# Revit family: HOSPIVAC 3 SIRELLA
name_source: partatom
category: Equipement de génie climatique
revit_build: Autodesk Revit 2018 (Build: 20170223_1515(x64)
units: mm (PartAtom-declared; Revit-internal decimal feet)

## family parameters
Basée sur le plan de construction = Non
Classification = Aucun
Cote de connecteur circulaire = Utiliser le diamètre
Couper avec des vides une fois chargée = Non
Partagée = Non
Point de calcul de pièce = Non
Toujours verticalement = Oui
Type d'élément = Normal

## types (4) — shared parameters
ANGLE = 60.00°
BRANCHEMENT_TERRE = Oui
COS_PHI = 0.9
DESCR_ALIM_X = Alimentation X ; 4G2.5mm²
DIAM_REFOUL_VIDE = 40 mm  [stored 0.131234 ft]
DOUBLE_ALIMENTATION = Oui
ENTRAXE_CANA_ASPI = 600 mm  [stored 1.9685 ft]
EP.VIROLE = 3 mm  [stored 0.00984252 ft]
FREQUENCE = 50 Hz
Fabricant = MIL'S
HAUT_ASPI = 60 mm  [stored 0.19685 ft]
HAUT_CANA_ASPI = 1500 mm
HAUT_CANA_FILTRE = 30 mm  [stored 0.0984252 ft]
HAUT_CANA_REFOUL = 820 mm  [stored 2.69029 ft]
HAUT_FIX = 15.2 mm
HAUT_TETE_FILTRE = 104 mm
HAUT_VIROLE = 155 mm  [stored 0.50853 ft]
LG_VIROLE = 2000 mm
LONG_ENTRAXE_PIED = 1500 mm
LONG_FOND = 145 mm
LONG_OFFSET_REFOUL = 220 mm  [stored 0.721785 ft]
LONG_SELLETTE_1 = 1995 mm
LONG_U = 650 mm  [stored 2.13255 ft]
Lien espace client = https://www.mils.fr
Modèle = HOSPIVAC
NBR_POLES = 3
NEUTRE = Oui
NIVEAU_SONORE(dB(A)) = 69
OFFSET2_LARG_ZONE_MAINT = 625 mm  [stored 2.05052 ft]
OFFSET_BRIDE = 200 mm  [stored 0.656168 ft]
OFFSET_CENTRAGE_PPE = 200 mm  [stored 0.656168 ft]
OFFSET_COUDE_CANA_FILTRE = 230 mm
OFFSET_HAUT_FILTRE = 725 mm  [stored 2.37861 ft]
OFFSET_HAUT_SELLETTE = 860 mm
OFFSET_LARG_1 = 182 mm  [stored 0.597113 ft]
OFFSET_LARG_2 = 332 mm
OFFSET_LARG_ASPI_PPE = 150 mm
OFFSET_LARG_FILTRE = 410 mm  [stored 1.34514 ft]
OFFSET_LARG_REFOUL = 294.5 mm
OFFSET_LONG_A1 = 222 mm
OFFSET_LONG_A2 = 481.8 mm
OFFSET_LONG_ASPI = 221 mm  [stored 0.725066 ft]
OFFSET_LONG_B1 = 822 mm  [stored 2.69685 ft]
OFFSET_LONG_B2 = 1081.8 mm
OFFSET_LONG_C1 = 1421.9 mm
OFFSET_LONG_C2 = 1681.8 mm
OFFSET_LONG_CANA_ASPI = 442 mm  [stored 1.45013 ft]
OFFSET_LONG_CANA_REFOUL = 1823 mm
OFFSET_LONG_FILTRE1 = 650 mm  [stored 2.13255 ft]
OFFSET_LONG_FILTRE2 = 40 mm  [stored 0.131234 ft]
OFFSET_LONG_PPE_A = 222 mm
OFFSET_PPE = 40 mm  [stored 0.131234 ft]
OFFSET_REFOUL = 501.5 mm  [stored 1.64534 ft]
OFFSET_REFOUL_PPE_B = 1449.2 mm
OFFSET_REFOUL_PPE_C = 1900 mm
OFFSET_SELLETTE_1 = 55 mm  [stored 0.180446 ft]
PROTEC_ELECT_X = Disjoncteur courbe D - 10 A
PROTEC_ELECT_Y = Disjoncteur courbe D - 16 A
TENSION_ALIM = 400 V
ØCANA = 45 mm  [stored 0.147638 ft]
ØVIROLE = 650 mm  [stored 2.13255 ft]

## per-type parameters (varying)
| type | DEBIT_ASPI_VIDE | DEBIT_REFOUL_VIDE | DEGAG_CALORIFIQUE(kJ/h) | DESCR_ALIM_Y | DESCR_ASPI | DESCR_REFOUL | DIAM_ASPI_VIDE | ENTRAXE_ALIM_ELEC | HAUTEUR | HAUT_FILTRE | LARGEUR | LONGUEUR | OFFSET1_LARG_ZONE_MAINT | OFFSET_REFOUL_PPE_A | POIDS(Kg) | PUISS_APPARENTE_X | PUISS_APPARENTE_Y | PUISS_ELECT_X | PUISS_ELECT_Y | TAILLE_POMPE | TYPE_COFFRET | ØFILTRE | ØPOT_FILTRE |
| c - HOSPIVAC 3 SL150.R | 420.0 m³/h | 420.0 m³/h | 37208 | Alimentation X ; 4G6mm² | Aspiration Vide ; 3x140 m³/h ; G 2" FEM | Refoulement Vide ; 3x140 m³/h ; G 1"1/2 MAL | 50 mm  [stored 0.164042 ft] | 1385 mm | 1560 mm | 380 mm  [stored 1.24672 ft] | 1350 mm | 2300 mm | 697.5 mm | 790 mm | 860 mm | 3333 VA | 6667 VA | 3 kW | 6 kW | SIRELLA SLR : SL150.R | COFFRET ELEC STANDARD PM2 : COFFRET PM2 600x300x300 | 195 mm  [stored 0.639764 ft] | 150 mm |
| a - HOSPIVAC 3 SL100.R | 270.0 m³/h | 270.0 m³/h | 27286 | Alimentation Y ; 4G6mm² | Aspiration Vide ; 3x90 m³/h ; G 2" FEM | Refoulement Vide ; 3x90 m³/h ; G 1"1/2 MAL | 50 mm  [stored 0.164042 ft] | 526 mm  [stored 1.72572 ft] | 1500 mm | 425 mm  [stored 1.39436 ft] | 1100 mm | 2400 mm | 656 mm | 780 mm  [stored 2.55906 ft] | 830 mm | 2444 VA | 4889 VA | 2 kW | 4 kW | SIRELLA SLR : SL100.R | COFFRET ELEC STANDARD PM2 : COFFRET PM2 600x300x300 | 112 mm | 100 mm  [stored 0.328084 ft] |
| b - HOSPIVAC 3 RS SL100.R | 288.0 m³/h | 288.0 m³/h | 37208 | Alimentation Y ; 4G6mm² | Aspiration Vide ; 3x90 m³/h ; G 2" FEM | Refoulement Vide ; 3x90 m³/h ; G 1"1/2 MAL | 40 mm  [stored 0.131234 ft] | 526 mm  [stored 1.72572 ft] | 1700 mm | 425 mm  [stored 1.39436 ft] | 1350 mm | 2300 mm | 656 mm | 780 mm  [stored 2.55906 ft] | 830 mm | 3333 VA | 6667 VA | 3 kW | 6 kW | SIRELLA SLR : SL100.R | COFFRET ELEC STANDARD PM2 : COFFRET PM2 600x800x300 | 112 mm | 100 mm  [stored 0.328084 ft] |
| d - HOSPIVAC 3 RS SL150.R | 444.0 m³/h | 444.0 m³/h | 37208 | Alimentation X ; 4G6mm² | Aspiration Vide ; 3x140 m³/h ; G 2" FEM | Refoulement Vide ; 3x140 m³/h ; G 1"1/2 MAL | 40 mm  [stored 0.131234 ft] | 1385 mm | 1560 mm | 380 mm  [stored 1.24672 ft] | 1350 mm | 2300 mm | 697.5 mm | 790 mm | 860 mm | 3333 VA | 6667 VA | 3 kW | 6 kW | SIRELLA SLR : SL150.R | COFFRET ELEC STANDARD PM2 : COFFRET PM2 600x800x300 | 195 mm  [stored 0.639764 ft] | 150 mm |

note: [stored X ft] marks values corroborated as IEEE doubles in the binary element streams (Revit-internal decimal feet)
